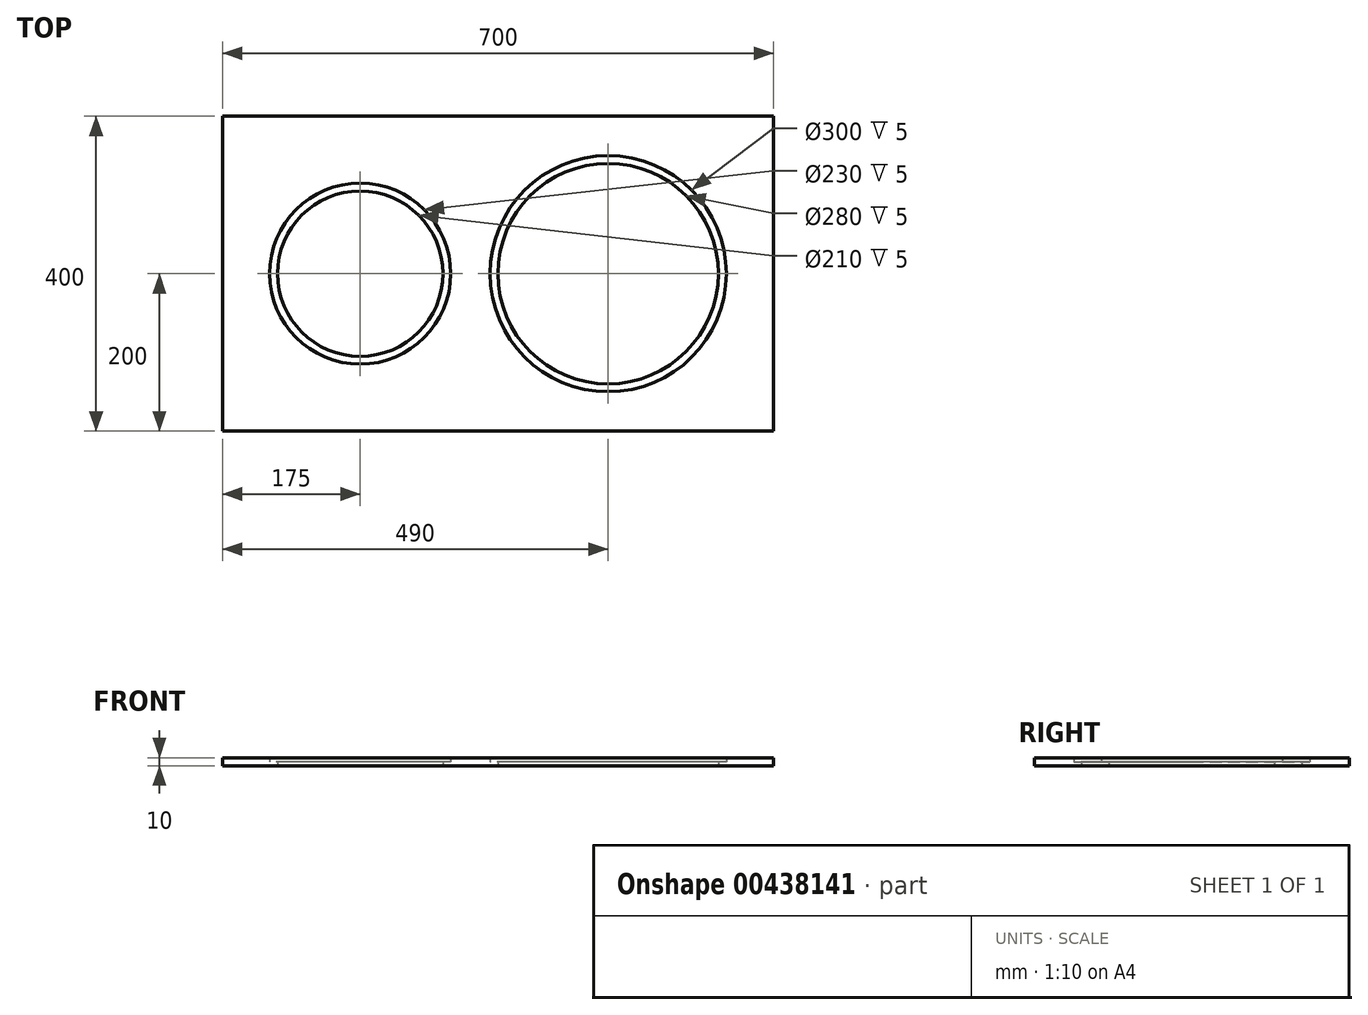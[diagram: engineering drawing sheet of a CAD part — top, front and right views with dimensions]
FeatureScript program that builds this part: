
annotation { "Feature Type Name" : "Feature", "Feature Type Description" : "" }
export const myFeature = defineFeature(function(context is Context, id is Id, definition is map)
    precondition{}
    {
        {
            var Q0;
            Q0=qCreatedBy(makeId("Top.planeOp"),FACE);
            var sketch = newSketch(context, id + "F0", { "sketchPlane" : qUnion([Q0])});
            skLineSegment(sketch, "E0.bottom", {"start": v(350, 200) * mm, "end": v(-350, 200) * mm});
            skLineSegment(sketch, "E0.top", {"start": v(350, -200) * mm, "end": v(-350, -200) * mm});
            skLineSegment(sketch, "E0.left", {"start": v(350, 200) * mm, "end": v(350, -200) * mm});
            skLineSegment(sketch, "E0.right", {"start": v(-350, 200) * mm, "end": v(-350, -200) * mm});
            skPoint(sketch, "E0.middle", {"position": v(0, 0) * mm});
            skLineSegment(sketch, "E1", {"start": v(-350, 0) * mm, "end": v(350, 0) * mm, "construction": true});
            skLineSegment(sketch, "E2", {"start": v(0, -200) * mm, "end": v(0, 200) * mm, "construction": true});
            skCircle(sketch, "E3", {"center": v(140, 0) * mm, "radius": 150 * mm});
            skCircle(sketch, "E4", {"center": v(-175, 0) * mm, "radius": 115 * mm});
            skCircle(sketch, "E5", {"center": v(140, 0) * mm, "radius": 140 * mm});
            skCircle(sketch, "E6", {"center": v(-175, 0) * mm, "radius": 105 * mm});
            skSolve(sketch);
        }
        {
            var Q0;
            Q0=makeQuery(id+"F0.imprint","IMPRINT",FACE,{"disambiguationData":[TD([[makeQuery(id+"F0.imprint","IMPRINT",EDGE,{"derivedFrom":sQuery(id+"F0.wireOp",EDGE,"E0.bottom")}),1.0]])]});
            extrude(context, id + "F1", {"entities" : qUnion([Q0]), "depth" : 10 * mm});
        }
        {
            var Q0;
            Q0=makeQuery(id+"F0.imprint","IMPRINT",FACE,{"disambiguationData":[TD([[makeQuery(id+"F0.imprint","IMPRINT",EDGE,{"derivedFrom":sQuery(id+"F0.wireOp",EDGE,"E4")}),1.0]])]});
            var Q1;
            Q1=makeQuery(id+"F0.imprint","IMPRINT",FACE,{"disambiguationData":[TD([[makeQuery(id+"F0.imprint","IMPRINT",EDGE,{"derivedFrom":sQuery(id+"F0.wireOp",EDGE,"E3")}),1.0]])]});
            extrude(context, id + "F2", {"entities" : qUnion([Q0, Q1]), "operationType" : NewBodyOperationType.ADD, "depth" : 5 * mm});
        }
    });
